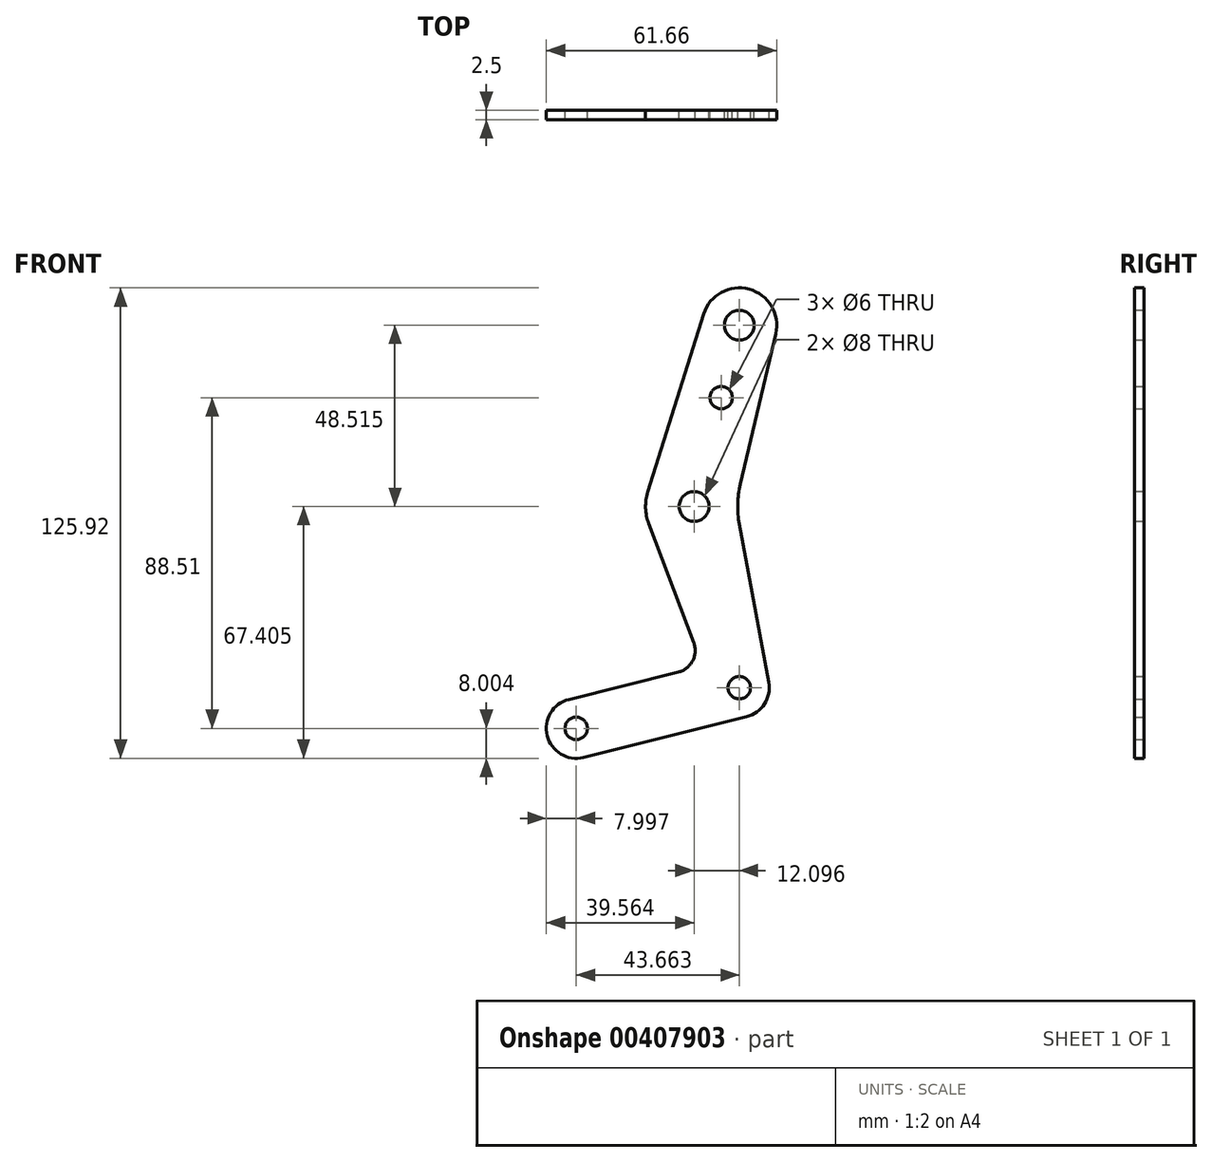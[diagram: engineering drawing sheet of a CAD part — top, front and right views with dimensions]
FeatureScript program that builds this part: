
annotation { "Feature Type Name" : "Feature", "Feature Type Description" : "" }
export const myFeature = defineFeature(function(context is Context, id is Id, definition is map)
    precondition{}
    {
        {
            var Q0;
            Q0=qCreatedBy(makeId("Front.planeOp"),FACE);
            var sketch = newSketch(context, id + "F0", { "sketchPlane" : qUnion([Q0])});
            skCircle(sketch, "E0", {"center": v(0, 0) * mm, "radius": 3 * mm});
            skCircle(sketch, "E1", {"center": v(-43.66, -10.89) * mm, "radius": 3 * mm});
            skCircle(sketch, "E2", {"center": v(-12.1, 48.51) * mm, "radius": 4 * mm});
            skCircle(sketch, "E3", {"center": v(0, 97.03) * mm, "radius": 4 * mm});
            skCircle(sketch, "E4", {"center": v(-4.84, 77.62) * mm, "radius": 3 * mm});
            skLineSegment(sketch, "E5", {"start": v(-12.1, 48.51) * mm, "end": v(0, 0) * mm, "construction": true});
            skLineSegment(sketch, "E6", {"start": v(-12.1, 48.51) * mm, "end": v(0, 97.03) * mm, "construction": true});
            skLineSegment(sketch, "E7", {"start": v(-43.66, -10.89) * mm, "end": v(0, 0) * mm, "construction": true});
            skLineSegment(sketch, "E8", {"start": v(-41.73, -18.65) * mm, "end": v(1.94, -7.76) * mm});
            skArc(sketch, "E9", {"start": v(1.94, -7.76) * mm, "mid": v(6.73, -4.33) * mm, "end": v(7.87, 1.46) * mm});
            skArc(sketch, "E10", {"start": v(-41.73, -18.65) * mm, "mid": v(-51.43, -12.82) * mm, "end": v(-45.6, -3.12) * mm});
            skArc(sketch, "E11", {"start": v(0.25, 54.47) * mm, "mid": v(-0.43, 49.13) * mm, "end": v(0, 43.76) * mm});
            skArc(sketch, "E12", {"start": v(-24.5, 52.41) * mm, "mid": v(-25.1, 48.14) * mm, "end": v(-24.25, 43.9) * mm});
            skArc(sketch, "E13", {"start": v(-9.54, 100.03) * mm, "mid": v(2.65, 106.67) * mm, "end": v(9.73, 94.74) * mm});
            skArc(sketch, "E14", {"start": v(-12.2, 12.11) * mm, "mid": v(-12.5, 7.2) * mm, "end": v(-16.36, 4.17) * mm});
            skLineSegment(sketch, "E15", {"start": v(-45.6, -3.12) * mm, "end": v(-16.36, 4.17) * mm});
            skLineSegment(sketch, "E16", {"start": v(-24.25, 43.9) * mm, "end": v(-12.2, 12.11) * mm});
            skLineSegment(sketch, "E17", {"start": v(-24.5, 52.41) * mm, "end": v(-9.54, 100.03) * mm});
            skLineSegment(sketch, "E18", {"start": v(9.73, 94.74) * mm, "end": v(0.25, 54.47) * mm});
            skLineSegment(sketch, "E19", {"start": v(0, 43.76) * mm, "end": v(7.87, 1.46) * mm});
            skSolve(sketch);
        }
        {
            var Q0;
            Q0 = qSketchRegion(id + "F0", true);
            extrude(context, id + "F1", {"entities" : qUnion([Q0]), "depth" : 2.5 * mm});
        }
    });
